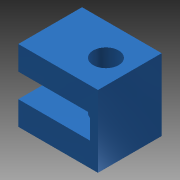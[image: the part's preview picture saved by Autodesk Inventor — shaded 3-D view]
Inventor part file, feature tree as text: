
AUTODESK INVENTOR PART (.ipt)
format: ipt  version: 2013 SP2 (Build 170200200, 200)  size: 92,672 bytes
history: native  units: in
note: dims shown in document units (in); Inventor stores cm internally (conversion verified against a paired STEP export)
features: extrude x2, sketch x2
ambient origin geometry x8: Origin, YZ Plane, XZ Plane, XY Plane, X Axis, Y Axis, Z Axis, Center Point
bodies: Solid1 (feature_tree)
feature tree (4):
  extrude  "Extrusion1"  Depth=0.3937in
  extrude  "Extrusion2"  Depth=0.1181in
  sketch  "Sketch1"  dims[d0=0.1181in d1=0.3937in]
  sketch  "Sketch2"  dims[d2=0.1181in d3=0.1181in d4=0.0394in d5=0.315in d6=0.0in d7=0.126in d8=0.1181in d9=0.3937in d10=0.0in]
